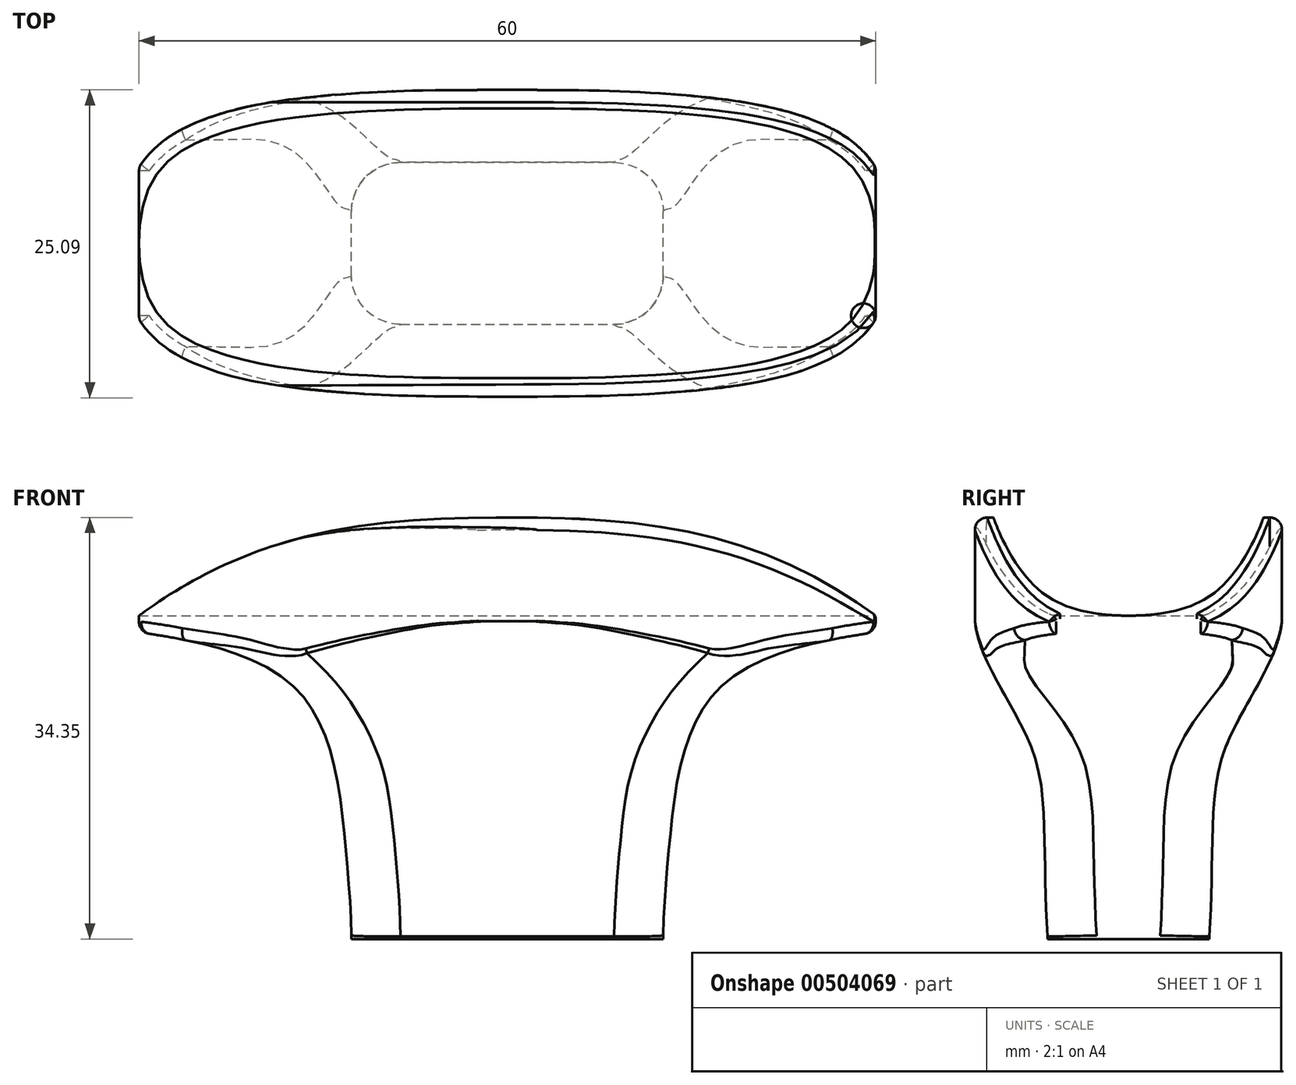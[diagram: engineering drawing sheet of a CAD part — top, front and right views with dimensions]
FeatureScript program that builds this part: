
annotation { "Feature Type Name" : "Feature", "Feature Type Description" : "" }
export const myFeature = defineFeature(function(context is Context, id is Id, definition is map)
    precondition{}
    {
        {
            var Q0;
            Q0=qCreatedBy(makeId("Front.planeOp"),FACE);
            var sketch = newSketch(context, id + "F0", { "sketchPlane" : qUnion([Q0])});
            skLineSegment(sketch, "E0", {"start": v(-30, 37.85) * mm, "end": v(30, 37.85) * mm, "construction": true});
            skFitSpline(sketch, "E1", {"points": [v(-30, 37.85) * mm, v(0, 45.85) * mm, v(30, 37.85) * mm], "startDerivative": vector(60, 44.44) * mm, "endDerivative": vector(60, -44.44) * mm});
            skLineSegment(sketch, "E2", {"start": v(0, 53.03) * mm, "end": v(0, -7.37) * mm, "construction": true});
            skLineSegment(sketch, "E3", {"start": v(-30, 37.85) * mm, "end": v(-30, 36.5) * mm});
            skFitSpline(sketch, "E4", {"points": [v(-30, 36.5) * mm, v(-17.05, 31.72) * mm, v(-13.22, 19.43) * mm, v(-12.7, 11.5) * mm], "startDerivative": vector(35.35, -5.31) * mm, "endDerivative": vector(0.02, -23.73) * mm});
            skLineSegment(sketch, "E5", {"start": v(-12.7, 11.5) * mm, "end": v(0, 11.5) * mm});
            skLineSegment(sketch, "E6.MirrorCS", {"start": v(30, 37.85) * mm, "end": v(30, 36.5) * mm});
            skFitSpline(sketch, "E7.MirrorCS", {"points": [v(30, 36.5) * mm, v(17.05, 31.72) * mm, v(13.22, 19.43) * mm, v(12.7, 11.5) * mm], "startDerivative": vector(-35.35, -5.31) * mm, "endDerivative": vector(-0.02, -23.73) * mm});
            skLineSegment(sketch, "E8.MirrorCS", {"start": v(12.7, 11.5) * mm, "end": v(0, 11.5) * mm});
            skSolve(sketch);
        }
        {
            var Q0;
            Q0 = qSketchRegion(id + "F0", true);
            extrude(context, id + "F1", {"entities" : qUnion([Q0]), "depth" : 25 * mm});
        }
        {
            var Q0;
            Q0=qCreatedBy(makeId("Right.planeOp"),FACE);
            var sketch = newSketch(context, id + "F2", { "sketchPlane" : qUnion([Q0])});
            skFitSpline(sketch, "E9.0.0", {"points": [v(0, 37.85) * mm, v(0, 40.51) * mm, v(0, 43.18) * mm, v(0, 45.85) * mm], "construction": true});
            skLineSegment(sketch, "E9.0.1", {"start": v(0, 37.85) * mm, "end": v(-25, 37.85) * mm, "construction": true});
            skFitSpline(sketch, "E9.0.2", {"points": [v(-25, 37.85) * mm, v(-25, 40.51) * mm, v(-25, 43.18) * mm, v(-25, 45.85) * mm], "construction": true});
            skLineSegment(sketch, "E9.0.3", {"start": v(-25, 37.85) * mm, "end": v(0, 37.85) * mm, "construction": true});
            skLineSegment(sketch, "E10", {"start": v(-12.5, 37.85) * mm, "end": v(-12.5, 47.5) * mm, "construction": true});
            skFitSpline(sketch, "E11", {"points": [v(-25, 37.85) * mm, v(-20.62, 27.63) * mm, v(-19.1, 11.72) * mm], "startDerivative": vector(-0.67, -19.89) * mm, "endDerivative": vector(2.62, -48.75) * mm});
            skFitSpline(sketch, "E12.MirrorCS", {"points": [v(0, 37.85) * mm, v(-4.38, 27.63) * mm, v(-5.9, 11.72) * mm], "startDerivative": vector(0.67, -19.89) * mm, "endDerivative": vector(-2.62, -48.75) * mm});
            skLineSegment(sketch, "E13", {"start": v(0, 37.85) * mm, "end": v(3.77, 37.85) * mm});
            skLineSegment(sketch, "E14", {"start": v(3.77, 37.85) * mm, "end": v(3.77, 8.57) * mm});
            skLineSegment(sketch, "E15", {"start": v(3.77, 8.57) * mm, "end": v(-5.9, 8.57) * mm});
            skLineSegment(sketch, "E16", {"start": v(-5.9, 8.57) * mm, "end": v(-5.9, 11.72) * mm});
            skLineSegment(sketch, "E17", {"start": v(-19.1, 11.72) * mm, "end": v(-19.1, 8.48) * mm});
            skLineSegment(sketch, "E18", {"start": v(-19.1, 8.48) * mm, "end": v(-28.34, 8.48) * mm});
            skLineSegment(sketch, "E19", {"start": v(-28.34, 8.48) * mm, "end": v(-28.34, 37.85) * mm});
            skLineSegment(sketch, "E20", {"start": v(-28.34, 37.85) * mm, "end": v(-25, 37.85) * mm});
            skFitSpline(sketch, "E21", {"points": [v(-23.5, 45.83) * mm, v(-20.96, 41.15) * mm, v(-12.5, 37.85) * mm], "startDerivative": vector(4.03, -11.03) * mm, "endDerivative": vector(25.89, 0) * mm});
            skFitSpline(sketch, "E22.MirrorCS", {"points": [v(-1.5, 45.83) * mm, v(-4.04, 41.15) * mm, v(-12.5, 37.85) * mm], "startDerivative": vector(-4.03, -11.03) * mm, "endDerivative": vector(-25.89, 0) * mm});
            skLineSegment(sketch, "E23", {"start": v(-23.5, 45.83) * mm, "end": v(-23.5, 46.98) * mm});
            skLineSegment(sketch, "E24", {"start": v(-23.5, 46.98) * mm, "end": v(-12.5, 46.98) * mm});
            skLineSegment(sketch, "E25.MirrorCS", {"start": v(-1.5, 46.98) * mm, "end": v(-12.5, 46.98) * mm});
            skLineSegment(sketch, "E26.MirrorCS", {"start": v(-1.5, 45.83) * mm, "end": v(-1.5, 46.98) * mm});
            skSolve(sketch);
        }
        {
            var Q0;
            Q0 = qSketchRegion(id + "F2", true);
            extrude(context, id + "F3", {"entities" : qUnion([Q0]), "operationType" : NewBodyOperationType.REMOVE, "endBound" : BoundingType.THROUGH_ALL, "oppositeDirection" : true, "depth" : 25 * mm, "hasSecondDirection" : true, "secondDirectionBound" : SecondDirectionBoundingType.THROUGH_ALL, "secondDirectionOppositeDirection" : false, "secondDirectionDepth" : 25 * mm});
        }
        {
            var Q0;
            Q0=qCreatedBy(makeId("Top.planeOp"),FACE);
            var sketch = newSketch(context, id + "F4", { "sketchPlane" : qUnion([Q0])});
            skFitSpline(sketch, "E27.0", {"points": [v(-31.27, -9.73) * mm, v(-31.3, -9.87) * mm, v(-31.33, -10.13) * mm, v(-31.37, -10.5) * mm, v(-31.4, -10.84) * mm, v(-31.41, -11.3) * mm, v(-31.43, -11.85) * mm, v(-31.43, -12.28) * mm, v(-31.43, -12.5) * mm]});
            skFitSpline(sketch, "E27.1", {"points": [v(-31.43, -12.5) * mm, v(-31.43, -12.72) * mm, v(-31.43, -13.15) * mm, v(-31.41, -13.7) * mm, v(-31.4, -14.16) * mm, v(-31.37, -14.5) * mm, v(-31.33, -14.87) * mm, v(-31.3, -15.13) * mm, v(-31.27, -15.27) * mm]});
            skFitSpline(sketch, "E27.2", {"points": [v(-31.5, -12.5) * mm, v(-31.5, -12.1) * mm, v(-31.48, -11.31) * mm, v(-31.37, -10.32) * mm, v(-31.24, -9.52) * mm, v(-31.1, -8.9) * mm, v(-30.93, -8.3) * mm, v(-30.71, -7.71) * mm, v(-30.46, -7.14) * mm, v(-30.17, -6.58) * mm, v(-29.83, -6.04) * mm, v(-29.45, -5.54) * mm, v(-29.04, -5.08) * mm, v(-28.61, -4.66) * mm, v(-28.15, -4.27) * mm, v(-27.53, -3.81) * mm, v(-26.73, -3.32) * mm, v(-25.76, -2.84) * mm, v(-24.77, -2.43) * mm, v(-23.43, -1.96) * mm, v(-21.73, -1.5) * mm, v(-19.66, -1.07) * mm, v(-17.9, -0.8) * mm, v(-16.47, -0.63) * mm, v(-15.04, -0.48) * mm, v(-13.25, -0.33) * mm, v(-10.38, -0.16) * mm, v(-6.78, -0.05) * mm, v(-3.89, -0.01) * mm, v(-2.44, 0) * mm]});
            skFitSpline(sketch, "E27.3", {"points": [v(-31.5, -12.5) * mm, v(-31.5, -12.9) * mm, v(-31.48, -13.69) * mm, v(-31.37, -14.68) * mm, v(-31.24, -15.48) * mm, v(-31.1, -16.1) * mm, v(-30.93, -16.7) * mm, v(-30.71, -17.29) * mm, v(-30.46, -17.86) * mm, v(-30.17, -18.42) * mm, v(-29.83, -18.96) * mm, v(-29.45, -19.46) * mm, v(-29.04, -19.92) * mm, v(-28.61, -20.34) * mm, v(-28.15, -20.73) * mm, v(-27.53, -21.19) * mm, v(-26.73, -21.68) * mm, v(-25.76, -22.16) * mm, v(-24.77, -22.57) * mm, v(-23.43, -23.04) * mm, v(-21.73, -23.5) * mm, v(-19.66, -23.93) * mm, v(-17.9, -24.2) * mm, v(-16.47, -24.37) * mm, v(-15.04, -24.52) * mm, v(-13.25, -24.67) * mm, v(-10.38, -24.84) * mm, v(-6.78, -24.95) * mm, v(-3.89, -24.99) * mm, v(-2.44, -25) * mm]});
            skFitSpline(sketch, "E27.4", {"points": [v(30, -25) * mm, v(10, -25) * mm, v(-10, -25) * mm, v(-30, -25) * mm]});
            skFitSpline(sketch, "E27.5", {"points": [v(2.44, -25) * mm, v(3.89, -24.99) * mm, v(6.78, -24.95) * mm, v(10.37, -24.84) * mm, v(13.23, -24.67) * mm, v(15.37, -24.5) * mm, v(17.5, -24.26) * mm, v(19.63, -23.93) * mm, v(21.72, -23.51) * mm, v(23.75, -22.95) * mm, v(25.42, -22.33) * mm, v(26.73, -21.68) * mm, v(27.7, -21.1) * mm, v(28.47, -20.48) * mm, v(29.04, -19.92) * mm, v(29.45, -19.46) * mm, v(29.83, -18.96) * mm, v(30.17, -18.42) * mm, v(30.46, -17.86) * mm, v(30.71, -17.29) * mm, v(30.92, -16.7) * mm, v(31.1, -16.1) * mm, v(31.24, -15.49) * mm, v(31.37, -14.68) * mm, v(31.48, -13.69) * mm, v(31.5, -12.9) * mm, v(31.5, -12.5) * mm]});
            skFitSpline(sketch, "E27.6", {"points": [v(30, 0) * mm, v(10, 0) * mm, v(-10, 0) * mm, v(-30, 0) * mm]});
            skFitSpline(sketch, "E27.7", {"points": [v(2.44, 0) * mm, v(3.89, -0.01) * mm, v(6.78, -0.05) * mm, v(10.37, -0.16) * mm, v(13.23, -0.33) * mm, v(15.37, -0.5) * mm, v(17.5, -0.74) * mm, v(19.63, -1.07) * mm, v(21.72, -1.49) * mm, v(23.75, -2.05) * mm, v(25.42, -2.67) * mm, v(26.73, -3.32) * mm, v(27.7, -3.9) * mm, v(28.47, -4.52) * mm, v(29.04, -5.08) * mm, v(29.45, -5.54) * mm, v(29.83, -6.04) * mm, v(30.17, -6.58) * mm, v(30.46, -7.14) * mm, v(30.71, -7.71) * mm, v(30.92, -8.3) * mm, v(31.1, -8.9) * mm, v(31.24, -9.51) * mm, v(31.37, -10.32) * mm, v(31.48, -11.31) * mm, v(31.5, -12.1) * mm, v(31.5, -12.5) * mm]});
            skFitSpline(sketch, "E27.8", {"points": [v(31.43, -12.52) * mm, v(31.43, -12.3) * mm, v(31.43, -11.87) * mm, v(31.41, -11.32) * mm, v(31.4, -10.87) * mm, v(31.37, -10.52) * mm, v(31.33, -10.16) * mm, v(31.3, -9.9) * mm, v(31.27, -9.76) * mm]});
            skFitSpline(sketch, "E27.9", {"points": [v(31.27, -15.27) * mm, v(31.3, -15.14) * mm, v(31.33, -14.88) * mm, v(31.37, -14.51) * mm, v(31.4, -14.17) * mm, v(31.41, -13.72) * mm, v(31.43, -13.17) * mm, v(31.43, -12.73) * mm, v(31.43, -12.52) * mm]});
            skLineSegment(sketch, "E28.bottom", {"start": v(-36.17, 3.87) * mm, "end": v(35.29, 3.87) * mm});
            skLineSegment(sketch, "E28.top", {"start": v(-36.17, -28.98) * mm, "end": v(35.29, -28.98) * mm});
            skLineSegment(sketch, "E28.left", {"start": v(-36.17, 3.87) * mm, "end": v(-36.17, -28.98) * mm});
            skLineSegment(sketch, "E28.right", {"start": v(35.29, 3.87) * mm, "end": v(35.29, -28.98) * mm});
            skLineSegment(sketch, "E29", {"start": v(31.27, -9.73) * mm, "end": v(31.27, -9.76) * mm});
            skLineSegment(sketch, "E30", {"start": v(-2.44, -25) * mm, "end": v(-2.44, -25) * mm});
            skLineSegment(sketch, "E31", {"start": v(2.44, 0) * mm, "end": v(2.44, 0) * mm});
            skSolve(sketch);
        }
        {
            var Q0;
            Q0 = qSketchRegion(id + "F4", true);
            extrude(context, id + "F5", {"entities" : qUnion([Q0]), "operationType" : NewBodyOperationType.REMOVE, "endBound" : BoundingType.THROUGH_ALL, "depth" : 25 * mm});
        }
        {
            var Q0;
            Q0=makeQuery(id+"F3.boolean.opBoolean","INTERSECT",EDGE,{"derivedFrom":[makeQuery(id+"F1.opExtrude","SWEPT_FACE",FACE,{"disambiguationData":[OSD([sQuery(id+"F0.wireOp",EDGE,"E4")])]}),makeQuery(id+"F3.opExtrude","SWEPT_FACE",FACE,{"disambiguationData":[OSD([sQuery(id+"F2.wireOp",EDGE,"E12.MirrorCS")])]})]});
            var Q1;
            Q1=makeQuery(id+"F3.boolean.opBoolean","INTERSECT",EDGE,{"derivedFrom":[makeQuery(id+"F1.opExtrude","SWEPT_FACE",FACE,{"disambiguationData":[OSD([sQuery(id+"F0.wireOp",EDGE,"E4")])]}),makeQuery(id+"F3.opExtrude","SWEPT_FACE",FACE,{"disambiguationData":[OSD([sQuery(id+"F2.wireOp",EDGE,"E11")])]})]});
            var Q2;
            Q2=makeQuery(id+"F3.boolean.opBoolean","INTERSECT",EDGE,{"derivedFrom":[makeQuery(id+"F1.opExtrude","SWEPT_FACE",FACE,{"disambiguationData":[OSD([sQuery(id+"F0.wireOp",EDGE,"E7.MirrorCS")])]}),makeQuery(id+"F3.opExtrude","SWEPT_FACE",FACE,{"disambiguationData":[OSD([sQuery(id+"F2.wireOp",EDGE,"E11")])]})]});
            var Q3;
            Q3=makeQuery(id+"F3.boolean.opBoolean","INTERSECT",EDGE,{"derivedFrom":[makeQuery(id+"F1.opExtrude","SWEPT_FACE",FACE,{"disambiguationData":[OSD([sQuery(id+"F0.wireOp",EDGE,"E7.MirrorCS")])]}),makeQuery(id+"F3.opExtrude","SWEPT_FACE",FACE,{"disambiguationData":[OSD([sQuery(id+"F2.wireOp",EDGE,"E12.MirrorCS")])]})]});
            fillet(context, id + "F6", {"entities" : qUnion([Q0, Q1, Q2, Q3]), "radius" : 4 * mm, "tangentPropagation" : true, "allowEdgeOverflow" : false});
        }
        {
            var Q0;
            Q0=makeQuery(id+"F3.boolean.opBoolean","INTERSECT",EDGE,{"derivedFrom":[makeQuery(id+"F1.opExtrude","SWEPT_FACE",FACE,{"disambiguationData":[OSD([sQuery(id+"F0.wireOp",EDGE,"E4")])]}),makeQuery(id+"F3.opExtrude","SWEPT_FACE",FACE,{"disambiguationData":[OSD([sQuery(id+"F2.wireOp",EDGE,"E16")])]})]});
            var Q1;
            Q1=makeQuery(id+"F3.boolean.opBoolean","INTERSECT",EDGE,{"derivedFrom":[makeQuery(id+"F1.opExtrude","SWEPT_FACE",FACE,{"disambiguationData":[OSD([sQuery(id+"F0.wireOp",EDGE,"E4")])]}),makeQuery(id+"F3.opExtrude","SWEPT_FACE",FACE,{"disambiguationData":[OSD([sQuery(id+"F2.wireOp",EDGE,"E17")])]})]});
            var Q2;
            Q2=makeQuery(id+"F3.boolean.opBoolean","INTERSECT",EDGE,{"derivedFrom":[makeQuery(id+"F1.opExtrude","SWEPT_FACE",FACE,{"disambiguationData":[OSD([sQuery(id+"F0.wireOp",EDGE,"E7.MirrorCS")])]}),makeQuery(id+"F3.opExtrude","SWEPT_FACE",FACE,{"disambiguationData":[OSD([sQuery(id+"F2.wireOp",EDGE,"E17")])]})]});
            var Q3;
            Q3=makeQuery(id+"F3.boolean.opBoolean","INTERSECT",EDGE,{"derivedFrom":[makeQuery(id+"F1.opExtrude","SWEPT_FACE",FACE,{"disambiguationData":[OSD([sQuery(id+"F0.wireOp",EDGE,"E7.MirrorCS")])]}),makeQuery(id+"F3.opExtrude","SWEPT_FACE",FACE,{"disambiguationData":[OSD([sQuery(id+"F2.wireOp",EDGE,"E16")])]})]});
            fillet(context, id + "F7", {"entities" : qUnion([Q0, Q1, Q2, Q3]), "radius" : 4 * mm, "tangentPropagation" : true, "allowEdgeOverflow" : false});
        }
        {
            var Q0;
            Q0=makeQuery(id+"F1.opExtrude","CAP_EDGE",EDGE,{"disambiguationData":[OSD([sQuery(id+"F0.wireOp",EDGE,"E1")])],"isStart":true});
            var Q1;
            Q1=makeQuery(id+"F1.opExtrude","CAP_EDGE",EDGE,{"disambiguationData":[OSD([sQuery(id+"F0.wireOp",EDGE,"E1")])],"isStart":false});
            var Q2;
            Q2=makeQuery(id+"F1.opExtrude","SWEPT_EDGE",EDGE,{"disambiguationData":[OSD([sQuery(id+"F0.wireOp",EDGE,"E3"),sQuery(id+"F0.wireOp",EDGE,"E4")])]});
            var Q3;
            Q3=makeQuery(id+"F1.opExtrude","SWEPT_EDGE",EDGE,{"disambiguationData":[OSD([sQuery(id+"F0.wireOp",EDGE,"E6.MirrorCS"),sQuery(id+"F0.wireOp",EDGE,"E7.MirrorCS")])]});
            fillet(context, id + "F8", {"entities" : qUnion([Q0, Q1, Q2, Q3]), "radius" : 1 * mm, "tangentPropagation" : true, "allowEdgeOverflow" : false});
        }
        {
            var Q0;
            {var subQ0=sQuery(id+"F0.wireOp",EDGE,"E6.MirrorCS");var subQ1=sQuery(id+"F0.wireOp",EDGE,"E1");Q0=makeQuery(id+"F3.boolean.opBoolean","SPLIT",EDGE,{"disambiguationData":[TD([makeQuery(id+"F1.opExtrude","CAP_FACE",FACE,{"disambiguationData":[OSD([subQ1,sQuery(id+"F0.wireOp",EDGE,"E3"),sQuery(id+"F0.wireOp",EDGE,"E4"),sQuery(id+"F0.wireOp",EDGE,"E5"),subQ0,sQuery(id+"F0.wireOp",EDGE,"E7.MirrorCS"),sQuery(id+"F0.wireOp",EDGE,"E8.MirrorCS")])],"isStart":false})])],"derivedFrom":makeQuery(id+"F1.opExtrude","SWEPT_EDGE",EDGE,{"disambiguationData":[OSD([subQ1,subQ0])]})});}
            var Q1;
            {var subQ0=sQuery(id+"F0.wireOp",EDGE,"E6.MirrorCS");var subQ1=sQuery(id+"F0.wireOp",EDGE,"E1");Q1=makeQuery(id+"F3.boolean.opBoolean","SPLIT",EDGE,{"disambiguationData":[TD([makeQuery(id+"F1.opExtrude","CAP_FACE",FACE,{"disambiguationData":[OSD([subQ1,sQuery(id+"F0.wireOp",EDGE,"E3"),sQuery(id+"F0.wireOp",EDGE,"E4"),sQuery(id+"F0.wireOp",EDGE,"E5"),subQ0,sQuery(id+"F0.wireOp",EDGE,"E7.MirrorCS"),sQuery(id+"F0.wireOp",EDGE,"E8.MirrorCS")])],"isStart":true})])],"derivedFrom":makeQuery(id+"F1.opExtrude","SWEPT_EDGE",EDGE,{"disambiguationData":[OSD([subQ1,subQ0])]})});}
            fillet(context, id + "F9", {"entities" : qUnion([Q0, Q1]), "radius" : 0.5 * mm, "tangentPropagation" : true, "allowEdgeOverflow" : false});
        }
        {
            var Q0;
            Q0=makeQuery(id+"F5.boolean.opBoolean","INTERSECT",EDGE,{"derivedFrom":[makeQuery(id+"F1.opExtrude","SWEPT_FACE",FACE,{"disambiguationData":[OSD([sQuery(id+"F0.wireOp",EDGE,"E3")])]}),makeQuery(id+"F5.opExtrude","SWEPT_FACE",FACE,{"disambiguationData":[OSD([sQuery(id+"F4.wireOp",EDGE,"E27.2")])]})]});
            var Q1;
            Q1=makeQuery(id+"F8.opFillet","BLEND_EDGE",EDGE,{"blendedFrom":[makeQuery(id+"F1.opExtrude","SWEPT_EDGE",EDGE,{"disambiguationData":[OSD([sQuery(id+"F0.wireOp",EDGE,"E3"),sQuery(id+"F0.wireOp",EDGE,"E4")])]}),makeQuery(id+"F5.boolean.opBoolean","COPY",FACE,{"derivedFrom":makeQuery(id+"F5.opExtrude","SWEPT_FACE",FACE,{"disambiguationData":[OSD([sQuery(id+"F4.wireOp",EDGE,"E27.2")])]})})],"blendedInto":[makeQuery(id+"F5.boolean.opBoolean","COPY",FACE,{"derivedFrom":makeQuery(id+"F5.opExtrude","SWEPT_FACE",FACE,{"disambiguationData":[OSD([sQuery(id+"F4.wireOp",EDGE,"E27.2")])]})})]});
            var Q2;
            Q2=makeQuery(id+"F5.boolean.opBoolean","INTERSECT",EDGE,{"derivedFrom":[makeQuery(id+"F1.opExtrude","SWEPT_FACE",FACE,{"disambiguationData":[OSD([sQuery(id+"F0.wireOp",EDGE,"E3")])]}),makeQuery(id+"F5.opExtrude","SWEPT_FACE",FACE,{"disambiguationData":[OSD([sQuery(id+"F4.wireOp",EDGE,"E27.3")])]})]});
            fillet(context, id + "F10", {"entities" : qUnion([Q0, Q1, Q2]), "radius" : 1 * mm, "tangentPropagation" : true, "allowEdgeOverflow" : false});
        }
        {
            var Q0;
            Q0=makeQuery(id+"F6.opFillet","BLEND_EDGE",EDGE,{"blendedFrom":[makeQuery(id+"F3.boolean.opBoolean","INTERSECT",EDGE,{"derivedFrom":[makeQuery(id+"F1.opExtrude","SWEPT_FACE",FACE,{"disambiguationData":[OSD([sQuery(id+"F0.wireOp",EDGE,"E7.MirrorCS")])]}),makeQuery(id+"F3.opExtrude","SWEPT_FACE",FACE,{"disambiguationData":[OSD([sQuery(id+"F2.wireOp",EDGE,"E11")])]})]}),makeQuery(id+"F5.boolean.opBoolean","COPY",FACE,{"derivedFrom":makeQuery(id+"F5.opExtrude","SWEPT_FACE",FACE,{"disambiguationData":[OSD([sQuery(id+"F4.wireOp",EDGE,"E27.5")])]})})],"blendedInto":[makeQuery(id+"F5.boolean.opBoolean","COPY",FACE,{"derivedFrom":makeQuery(id+"F5.opExtrude","SWEPT_FACE",FACE,{"disambiguationData":[OSD([sQuery(id+"F4.wireOp",EDGE,"E27.5")])]})})]});
            var Q1;
            Q1=makeQuery(id+"F6.opFillet","BLEND_EDGE",EDGE,{"blendedFrom":[makeQuery(id+"F3.boolean.opBoolean","INTERSECT",EDGE,{"derivedFrom":[makeQuery(id+"F1.opExtrude","SWEPT_FACE",FACE,{"disambiguationData":[OSD([sQuery(id+"F0.wireOp",EDGE,"E7.MirrorCS")])]}),makeQuery(id+"F3.opExtrude","SWEPT_FACE",FACE,{"disambiguationData":[OSD([sQuery(id+"F2.wireOp",EDGE,"E12.MirrorCS")])]})]}),makeQuery(id+"F5.boolean.opBoolean","COPY",FACE,{"derivedFrom":makeQuery(id+"F5.opExtrude","SWEPT_FACE",FACE,{"disambiguationData":[OSD([sQuery(id+"F4.wireOp",EDGE,"E27.7")])]})})],"blendedInto":[makeQuery(id+"F5.boolean.opBoolean","COPY",FACE,{"derivedFrom":makeQuery(id+"F5.opExtrude","SWEPT_FACE",FACE,{"disambiguationData":[OSD([sQuery(id+"F4.wireOp",EDGE,"E27.7")])]})})]});
            fillet(context, id + "F11", {"entities" : qUnion([Q0, Q1]), "radius" : 1 * mm, "tangentPropagation" : true, "allowEdgeOverflow" : false});
        }
    });
